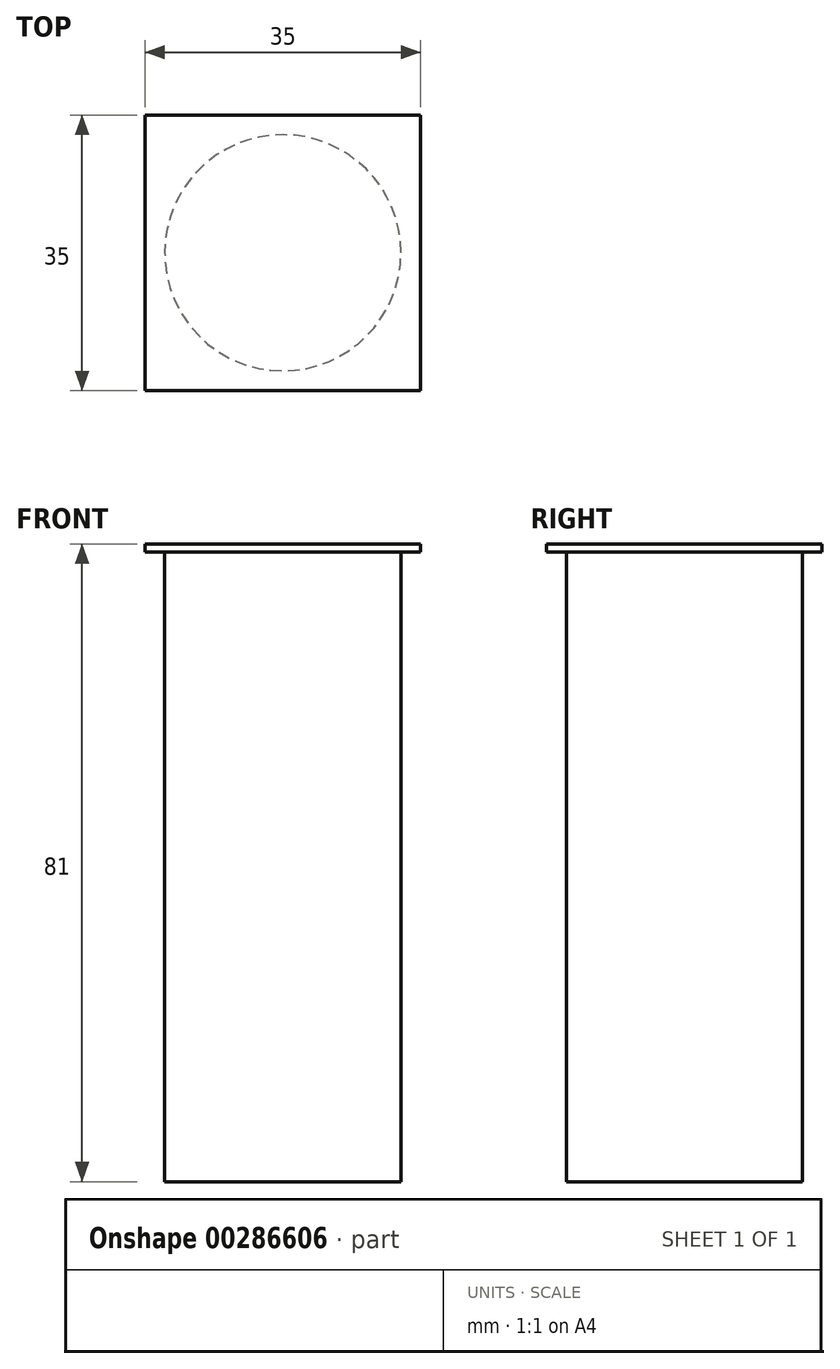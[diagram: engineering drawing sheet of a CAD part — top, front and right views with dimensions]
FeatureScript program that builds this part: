
annotation { "Feature Type Name" : "Feature", "Feature Type Description" : "" }
export const myFeature = defineFeature(function(context is Context, id is Id, definition is map)
    precondition{}
    {
        {
            var Q0;
            Q0=qCreatedBy(makeId("Top.planeOp"),FACE);
            var sketch = newSketch(context, id + "F0", { "sketchPlane" : qUnion([Q0])});
            skCircle(sketch, "E0", {"center": v(0, 0) * mm, "radius": 15 * mm});
            skSolve(sketch);
        }
        {
            var Q0;
            Q0=makeQuery(id+"F0.imprint","IMPRINT",FACE,{"disambiguationData":[TD([[makeQuery(id+"F0.imprint","IMPRINT",EDGE,{"derivedFrom":sQuery(id+"F0.wireOp",EDGE,"E0")}),1.0]])]});
            extrude(context, id + "F1", {"entities" : qUnion([Q0]), "depth" : 80 * mm});
        }
        {
            var Q0;
            Q0=makeQuery(id+"F1.opExtrude","CAP_FACE",FACE,{"disambiguationData":[OSD([sQuery(id+"F0.wireOp",EDGE,"E0")])],"isStart":false});
            var sketch = newSketch(context, id + "F2", { "sketchPlane" : qUnion([Q0])});
            skLineSegment(sketch, "E1.bottom", {"start": v(-17.5, 17.5) * mm, "end": v(17.5, 17.5) * mm});
            skLineSegment(sketch, "E1.top", {"start": v(-17.5, -17.5) * mm, "end": v(17.5, -17.5) * mm});
            skLineSegment(sketch, "E1.left", {"start": v(-17.5, 17.5) * mm, "end": v(-17.5, -17.5) * mm});
            skLineSegment(sketch, "E1.right", {"start": v(17.5, 17.5) * mm, "end": v(17.5, -17.5) * mm});
            skPoint(sketch, "E1.middle", {"position": v(0, 0) * mm});
            skSolve(sketch);
        }
        {
            var Q0;
            Q0=makeQuery(id+"F2.imprint","IMPRINT",FACE,{"disambiguationData":[TD([[makeQuery(id+"F2.imprint","IMPRINT",EDGE,{"derivedFrom":sQuery(id+"F2.wireOp",EDGE,"E1.bottom")}),-1.0]])]});
            var Q1;
            Q1=makeQuery(id+"F2.imprint","IMPRINT",FACE,{"disambiguationData":[TD([[makeQuery(id+"F2.imprint","IMPRINT",EDGE,{"derivedFrom":makeQuery(id+"F1.opExtrude","CAP_EDGE",EDGE,{"disambiguationData":[OSD([sQuery(id+"F0.wireOp",EDGE,"E0")])],"isStart":false})}),1.0]])]});
            extrude(context, id + "F3", {"entities" : qUnion([Q0, Q1]), "operationType" : NewBodyOperationType.ADD, "depth" : 1 * mm});
        }
    });
